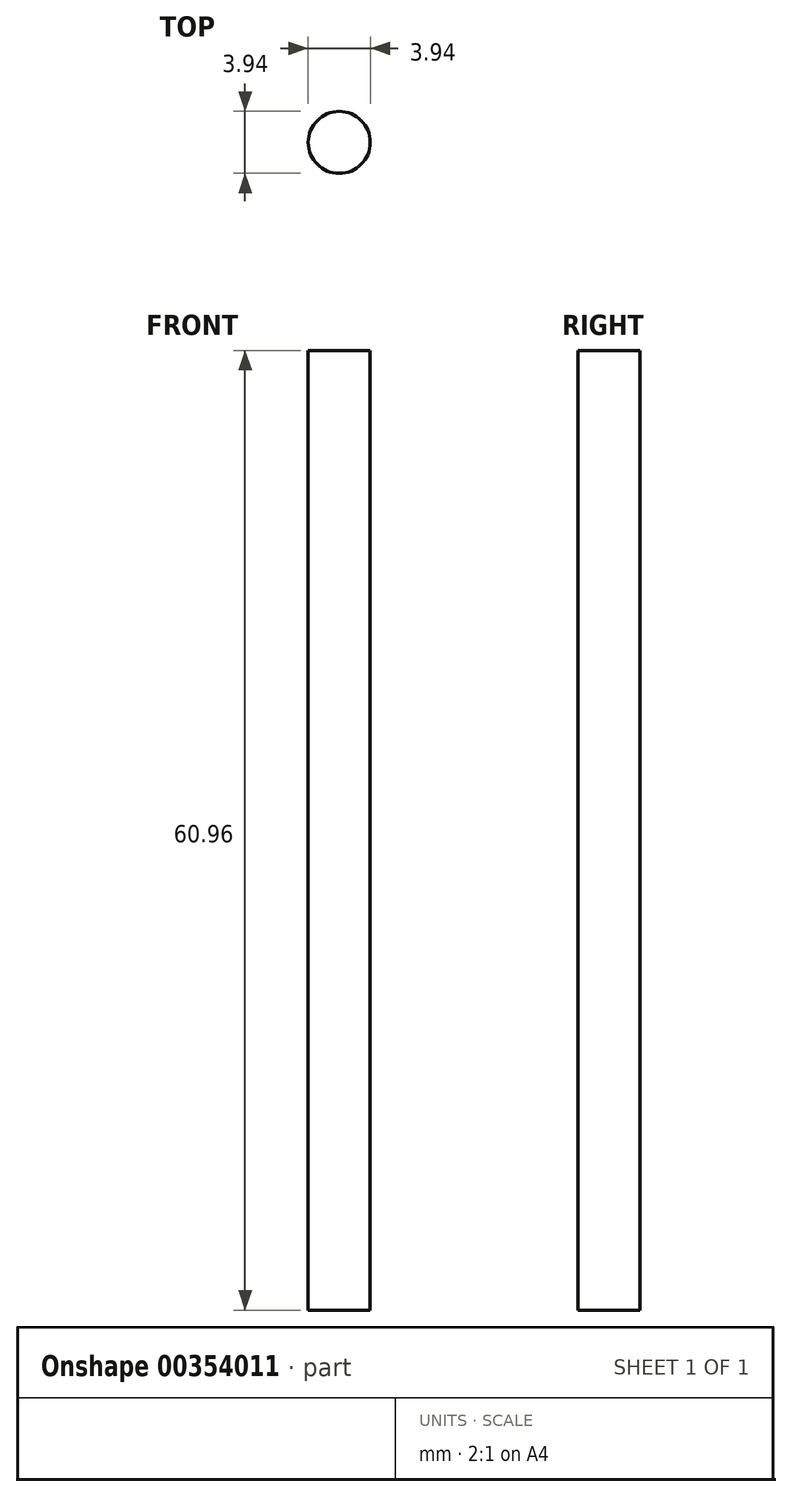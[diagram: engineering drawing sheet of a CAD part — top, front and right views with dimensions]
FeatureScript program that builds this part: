
annotation { "Feature Type Name" : "Feature", "Feature Type Description" : "" }
export const myFeature = defineFeature(function(context is Context, id is Id, definition is map)
    precondition{}
    {
        {
            var Q0;
            Q0=qCreatedBy(makeId("Top.planeOp"),FACE);
            var sketch = newSketch(context, id + "F0", { "sketchPlane" : qUnion([Q0])});
            skCircle(sketch, "E0", {"center": v(0, 0) * mm, "radius": 1.97 * mm});
            skSolve(sketch);
        }
        {
            var Q0;
            Q0=makeQuery(id+"F0.imprint","IMPRINT",FACE,{"disambiguationData":[TD([[makeQuery(id+"F0.imprint","IMPRINT",EDGE,{"derivedFrom":sQuery(id+"F0.wireOp",EDGE,"E0")}),1.0]])]});
            extrude(context, id + "F1", {"entities" : qUnion([Q0]), "depth" : 60.96 * mm});
        }
    });
